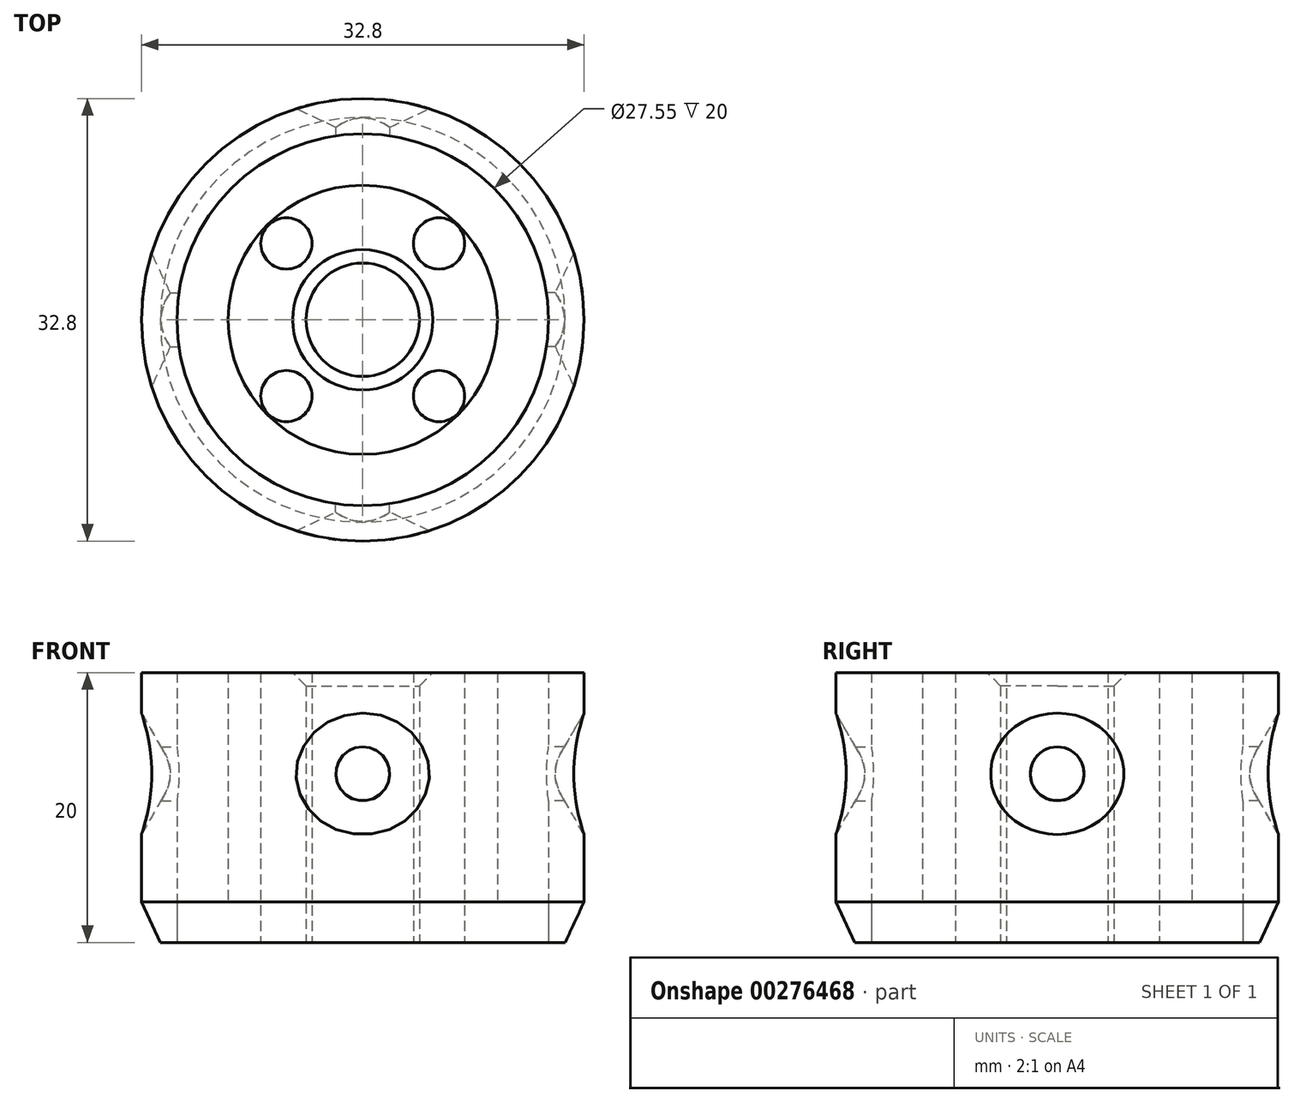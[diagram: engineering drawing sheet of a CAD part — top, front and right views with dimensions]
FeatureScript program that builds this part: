
annotation { "Feature Type Name" : "Feature", "Feature Type Description" : "" }
export const myFeature = defineFeature(function(context is Context, id is Id, definition is map)
    precondition{}
    {
        {
            var Q0;
            Q0=qCreatedBy(makeId("Top.planeOp"),FACE);
            var sketch = newSketch(context, id + "F0", { "sketchPlane" : qUnion([Q0])});
            skCircle(sketch, "E0", {"center": v(0, 0) * mm, "radius": 13.78 * mm});
            skCircle(sketch, "E1", {"center": v(0, 0) * mm, "radius": 3.35 * mm});
            skLineSegment(sketch, "E2", {"start": v(-2.3, -2.44) * mm, "end": v(1.68, -2.9) * mm});
            skSolve(sketch);
        }
        {
            var Q0;
            Q0=makeQuery(id+"F0.imprint","IMPRINT",FACE,{"disambiguationData":[TD([[makeQuery(id+"F0.imprint","IMPRINT",EDGE,{"derivedFrom":sQuery(id+"F0.wireOp",EDGE,"E0")}),1.0]])]});
            var sketch = newSketch(context, id + "F1", { "sketchPlane" : qUnion([Q0])});
            skCircle(sketch, "E3", {"center": v(0, 0) * mm, "radius": 16.4 * mm});
            skSolve(sketch);
        }
        {
            var Q0;
            Q0=makeQuery(id+"F1.imprint","IMPRINT",FACE,{"disambiguationData":[TD([[makeQuery(id+"F1.imprint","IMPRINT",EDGE,{"derivedFrom":sQuery(id+"F1.wireOp",EDGE,"E3")}),1.0]])]});
            var Q1;
            Q1=makeQuery(id+"F0.imprint","IMPRINT",FACE,{"disambiguationData":[TD([[makeQuery(id+"F0.imprint","IMPRINT",EDGE,{"derivedFrom":sQuery(id+"F0.wireOp",EDGE,"E0")}),1.0]])]});
            var Q2;
            {var subQ0=sQuery(id+"F0.wireOp",EDGE,"E2");Q2=makeQuery(id+"F0.imprint","IMPRINT",FACE,{"disambiguationData":[TD([[makeQuery(id+"F0.imprint","IMPRINT",EDGE,{"derivedFrom":subQ0}),1.0]])]});}
            var Q3;
            {var subQ0=sQuery(id+"F0.wireOp",EDGE,"E2");Q3=makeQuery(id+"F0.imprint","IMPRINT",FACE,{"disambiguationData":[TD([[makeQuery(id+"F0.imprint","IMPRINT",EDGE,{"derivedFrom":subQ0}),-1.0]])]});}
            extrude(context, id + "F2", {"entities" : qUnion([Q0, Q1, Q2, Q3]), "depth" : 20 * mm});
        }
        {
            var Q0;
            Q0=makeQuery(id+"F2.opExtrude","CAP_FACE",FACE,{"disambiguationData":[OSD([sQuery(id+"F0.wireOp",EDGE,"E0")])],"isStart":false});
            extrude(context, id + "F3", {"entities" : qUnion([Q0]), "operationType" : NewBodyOperationType.REMOVE, "oppositeDirection" : true, "depth" : 17 * mm});
        }
        {
            var Q0;
            Q0=makeQuery(id+"F2.opExtrude","CAP_FACE",FACE,{"disambiguationData":[OSD([sQuery(id+"F0.wireOp",EDGE,"E0")])],"isStart":true});
            var sketch = newSketch(context, id + "F4", { "sketchPlane" : qUnion([Q0])});
            skCircle(sketch, "E4", {"center": v(0, 0) * mm, "radius": 4.2 * mm});
            skLineSegment(sketch, "E5", {"start": v(4.2, 0) * mm, "end": v(-4.2, 0) * mm, "construction": true});
            skSolve(sketch);
        }
        {
            var Q0;
            Q0=makeQuery(id+"F4.imprint","IMPRINT",FACE,{"disambiguationData":[TD([[makeQuery(id+"F4.imprint","IMPRINT",EDGE,{"derivedFrom":sQuery(id+"F4.wireOp",EDGE,"E4")}),1.0]])]});
            extrude(context, id + "F5", {"entities" : qUnion([Q0]), "operationType" : NewBodyOperationType.REMOVE, "oppositeDirection" : true, "depth" : 9 * mm});
        }
        {
            var Q0;
            Q0=makeQuery(id+"F2.opExtrude","CAP_FACE",FACE,{"disambiguationData":[OSD([sQuery(id+"F0.wireOp",EDGE,"E0")])],"isStart":true});
            var sketch = newSketch(context, id + "F6", { "sketchPlane" : qUnion([Q0])});
            skLineSegment(sketch, "E6", {"start": v(0, 0) * mm, "end": v(-8, 0) * mm});
            skLineSegment(sketch, "E7", {"start": v(0, 0) * mm, "end": v(0, 8) * mm});
            skLineSegment(sketch, "E8", {"start": v(0, 0) * mm, "end": v(-5.66, 5.66) * mm});
            skLineSegment(sketch, "E9", {"start": v(0, 0) * mm, "end": v(5.66, -5.66) * mm});
            skLineSegment(sketch, "E10", {"start": v(0, 0) * mm, "end": v(-5.66, -5.66) * mm});
            skLineSegment(sketch, "E11", {"start": v(0, 0) * mm, "end": v(5.66, 5.66) * mm});
            skCircle(sketch, "E12", {"center": v(-5.66, 5.66) * mm, "radius": 1.9 * mm});
            skCircle(sketch, "E13", {"center": v(-5.66, -5.66) * mm, "radius": 1.9 * mm});
            skCircle(sketch, "E14", {"center": v(5.66, 5.66) * mm, "radius": 1.9 * mm});
            skCircle(sketch, "E15", {"center": v(5.66, -5.66) * mm, "radius": 1.9 * mm});
            skSolve(sketch);
        }
        {
            var Q0;
            Q0=makeQuery(id+"F6.imprint","IMPRINT",FACE,{"disambiguationData":[TD([[makeQuery(id+"F6.imprint","IMPRINT",EDGE,{"derivedFrom":sQuery(id+"F6.wireOp",EDGE,"E12")}),1.0]])]});
            var Q1;
            Q1=makeQuery(id+"F6.imprint","IMPRINT",FACE,{"disambiguationData":[TD([[makeQuery(id+"F6.imprint","IMPRINT",EDGE,{"derivedFrom":sQuery(id+"F6.wireOp",EDGE,"E13")}),1.0]])]});
            var Q2;
            Q2=makeQuery(id+"F6.imprint","IMPRINT",FACE,{"disambiguationData":[TD([[makeQuery(id+"F6.imprint","IMPRINT",EDGE,{"derivedFrom":sQuery(id+"F6.wireOp",EDGE,"E14")}),1.0]])]});
            var Q3;
            Q3=makeQuery(id+"F6.imprint","IMPRINT",FACE,{"disambiguationData":[TD([[makeQuery(id+"F6.imprint","IMPRINT",EDGE,{"derivedFrom":sQuery(id+"F6.wireOp",EDGE,"E15")}),1.0]])]});
            extrude(context, id + "F7", {"entities" : qUnion([Q0, Q1, Q2, Q3]), "operationType" : NewBodyOperationType.REMOVE, "oppositeDirection" : true, "depth" : 9 * mm});
        }
        {
            var Q0;
            Q0=qCreatedBy(makeId("Front.planeOp"),FACE);
            var sketch = newSketch(context, id + "F8", { "sketchPlane" : qUnion([Q0])});
            skLineSegment(sketch, "E16", {"start": v(0, 0) * mm, "end": v(0, 25) * mm});
            skCircle(sketch, "E17", {"center": v(0, 12.5) * mm, "radius": 2 * mm});
            skSolve(sketch);
        }
        {
            var Q0;
            Q0=qSketchRegion(id+"F8",true);
            extrude(context, id + "F9", {"entities" : qUnion([Q0]), "operationType" : NewBodyOperationType.REMOVE, "endBound" : BoundingType.THROUGH_ALL, "oppositeDirection" : true, "depth" : 25 * mm});
        }
        {
            var Q0;
            Q0=qCreatedBy(makeId("Front.planeOp"),FACE);
            var sketch = newSketch(context, id + "F10", { "sketchPlane" : qUnion([Q0])});
            skLineSegment(sketch, "E18", {"start": v(0, 0) * mm, "end": v(0, 25) * mm});
            skCircle(sketch, "E19", {"center": v(0, 12.5) * mm, "radius": 2 * mm});
            skSolve(sketch);
        }
        {
            var Q0;
            Q0=qSketchRegion(id+"F10",true);
            extrude(context, id + "F11", {"entities" : qUnion([Q0]), "operationType" : NewBodyOperationType.REMOVE, "endBound" : BoundingType.THROUGH_ALL, "depth" : 25 * mm});
        }
        {
            var Q0;
            Q0=qCreatedBy(makeId("Right.planeOp"),FACE);
            var sketch = newSketch(context, id + "F12", { "sketchPlane" : qUnion([Q0])});
            skLineSegment(sketch, "E20", {"start": v(0, 0) * mm, "end": v(0, 25) * mm});
            skCircle(sketch, "E21", {"center": v(0, 12.5) * mm, "radius": 2 * mm});
            skSolve(sketch);
        }
        {
            var Q0;
            Q0=qSketchRegion(id+"F12",true);
            extrude(context, id + "F13", {"entities" : qUnion([Q0]), "operationType" : NewBodyOperationType.REMOVE, "endBound" : BoundingType.THROUGH_ALL, "oppositeDirection" : true, "depth" : 25 * mm});
        }
        {
            var Q0;
            Q0=qCreatedBy(makeId("Right.planeOp"),FACE);
            var sketch = newSketch(context, id + "F14", { "sketchPlane" : qUnion([Q0])});
            skLineSegment(sketch, "E22", {"start": v(0, 0) * mm, "end": v(0, 25) * mm});
            skCircle(sketch, "E23", {"center": v(0, 12.5) * mm, "radius": 2 * mm});
            skSolve(sketch);
        }
        {
            var Q0;
            Q0=qSketchRegion(id+"F14",true);
            extrude(context, id + "F15", {"entities" : qUnion([Q0]), "operationType" : NewBodyOperationType.REMOVE, "endBound" : BoundingType.THROUGH_ALL, "depth" : 25 * mm});
        }
        {
            var Q0;
            Q0=makeQuery(id+"F3.boolean.opBoolean","COPY",FACE,{"derivedFrom":makeQuery(id+"F3.opExtrude","CAP_FACE",FACE,{"disambiguationData":[OSD([sQuery(id+"F0.wireOp",EDGE,"E0")])],"isStart":false})});
            var sketch = newSketch(context, id + "F16", { "sketchPlane" : qUnion([Q0])});
            skCircle(sketch, "E24", {"center": v(0, 0) * mm, "radius": 9.97 * mm});
            skSolve(sketch);
        }
        {
            var Q0;
            {var subQ1=makeQuery(id+"F3.boolean.opBoolean","COPY",FACE,{"derivedFrom":makeQuery(id+"F3.opExtrude","CAP_FACE",FACE,{"disambiguationData":[OSD([sQuery(id+"F0.wireOp",EDGE,"E0")])],"isStart":false})});Q0=makeQuery(id+"F16.imprint","IMPRINT",FACE,{"disambiguationData":[TD([[makeQuery(id+"F16.imprint","IMPRINT",EDGE,{"derivedFrom":makeQuery(id+"F5.boolean.opBoolean","INTERSECT",EDGE,{"derivedFrom":[subQ1,makeQuery(id+"F5.opExtrude","SWEPT_FACE",FACE,{"disambiguationData":[OSD([sQuery(id+"F4.wireOp",EDGE,"E4")])]})]})}),-1.0]])]});}
            extrude(context, id + "F17", {"entities" : qUnion([Q0]), "operationType" : NewBodyOperationType.ADD, "depth" : 17 * mm});
        }
        {
            var Q0;
            Q0=makeQuery(id+"F13.boolean.opBoolean","INTERSECT",EDGE,{"derivedFrom":[makeQuery(id+"F2.opExtrude","SWEPT_FACE",FACE,{"disambiguationData":[OSD([sQuery(id+"F1.wireOp",EDGE,"E3")])]}),makeQuery(id+"F13.opExtrude","SWEPT_FACE",FACE,{"disambiguationData":[OSD([sQuery(id+"F12.wireOp",EDGE,"E21")])]})]});
            var Q1;
            Q1=makeQuery(id+"F9.boolean.opBoolean","INTERSECT",EDGE,{"derivedFrom":[makeQuery(id+"F2.opExtrude","SWEPT_FACE",FACE,{"disambiguationData":[OSD([sQuery(id+"F1.wireOp",EDGE,"E3")])]}),makeQuery(id+"F9.opExtrude","SWEPT_FACE",FACE,{"disambiguationData":[OSD([sQuery(id+"F8.wireOp",EDGE,"E17")])]})]});
            var Q2;
            Q2=makeQuery(id+"F11.boolean.opBoolean","INTERSECT",EDGE,{"derivedFrom":[makeQuery(id+"F2.opExtrude","SWEPT_FACE",FACE,{"disambiguationData":[OSD([sQuery(id+"F1.wireOp",EDGE,"E3")])]}),makeQuery(id+"F11.opExtrude","SWEPT_FACE",FACE,{"disambiguationData":[OSD([sQuery(id+"F10.wireOp",EDGE,"E19")])]})]});
            var Q3;
            Q3=makeQuery(id+"F15.boolean.opBoolean","INTERSECT",EDGE,{"derivedFrom":[makeQuery(id+"F2.opExtrude","SWEPT_FACE",FACE,{"disambiguationData":[OSD([sQuery(id+"F1.wireOp",EDGE,"E3")])]}),makeQuery(id+"F15.opExtrude","SWEPT_FACE",FACE,{"disambiguationData":[OSD([sQuery(id+"F14.wireOp",EDGE,"E23")])]})]});
            chamfer(context, id + "F18", {"entities" : qUnion([Q0, Q1, Q2, Q3]), "chamferType" : ChamferType.OFFSET_ANGLE, "width" : 2.5 * mm, "oppositeDirection" : false, "angle" : 30 * degree, "tangentPropagation" : true});
        }
        {
            var Q0;
            Q0=makeQuery(id+"F2.opExtrude","CAP_EDGE",EDGE,{"disambiguationData":[OSD([sQuery(id+"F1.wireOp",EDGE,"E3")])],"isStart":true});
            chamfer(context, id + "F19", {"entities" : qUnion([Q0]), "chamferType" : ChamferType.OFFSET_ANGLE, "width" : 3 * mm, "oppositeDirection" : false, "angle" : 25 * degree, "tangentPropagation" : true});
        }
        {
            var Q0;
            Q0=makeQuery(id+"F17.opExtrude","CAP_EDGE",EDGE,{"disambiguationData":[OSD([sQuery(id+"F0.wireOp",EDGE,"E0"),sQuery(id+"F4.wireOp",EDGE,"E4")])],"isStart":false});
            var Q1;
            Q1=makeQuery(id+"F5.boolean.opBoolean","COPY",EDGE,{"derivedFrom":makeQuery(id+"F5.opExtrude","CAP_EDGE",EDGE,{"disambiguationData":[OSD([sQuery(id+"F4.wireOp",EDGE,"E4")])],"isStart":true})});
            var Q2;
            Q2=makeQuery(id+"F7.boolean.opBoolean","COPY",EDGE,{"derivedFrom":makeQuery(id+"F7.opExtrude","CAP_EDGE",EDGE,{"disambiguationData":[OSD([sQuery(id+"F6.wireOp",EDGE,"E12")])],"isStart":true})});
            var Q3;
            Q3=makeQuery(id+"F7.boolean.opBoolean","COPY",EDGE,{"derivedFrom":makeQuery(id+"F7.opExtrude","CAP_EDGE",EDGE,{"disambiguationData":[OSD([sQuery(id+"F6.wireOp",EDGE,"E13")])],"isStart":true})});
            var Q4;
            Q4=makeQuery(id+"F7.boolean.opBoolean","COPY",EDGE,{"derivedFrom":makeQuery(id+"F7.opExtrude","CAP_EDGE",EDGE,{"disambiguationData":[OSD([sQuery(id+"F6.wireOp",EDGE,"E14")])],"isStart":true})});
            var Q5;
            Q5=makeQuery(id+"F7.boolean.opBoolean","COPY",EDGE,{"derivedFrom":makeQuery(id+"F7.opExtrude","CAP_EDGE",EDGE,{"disambiguationData":[OSD([sQuery(id+"F6.wireOp",EDGE,"E15")])],"isStart":true})});
            chamfer(context, id + "F20", {"entities" : qUnion([Q0, Q1, Q2, Q3, Q4, Q5]), "chamferType" : ChamferType.OFFSET_ANGLE, "width" : 1 * mm, "oppositeDirection" : false, "angle" : 45 * degree, "tangentPropagation" : true});
        }
    });
